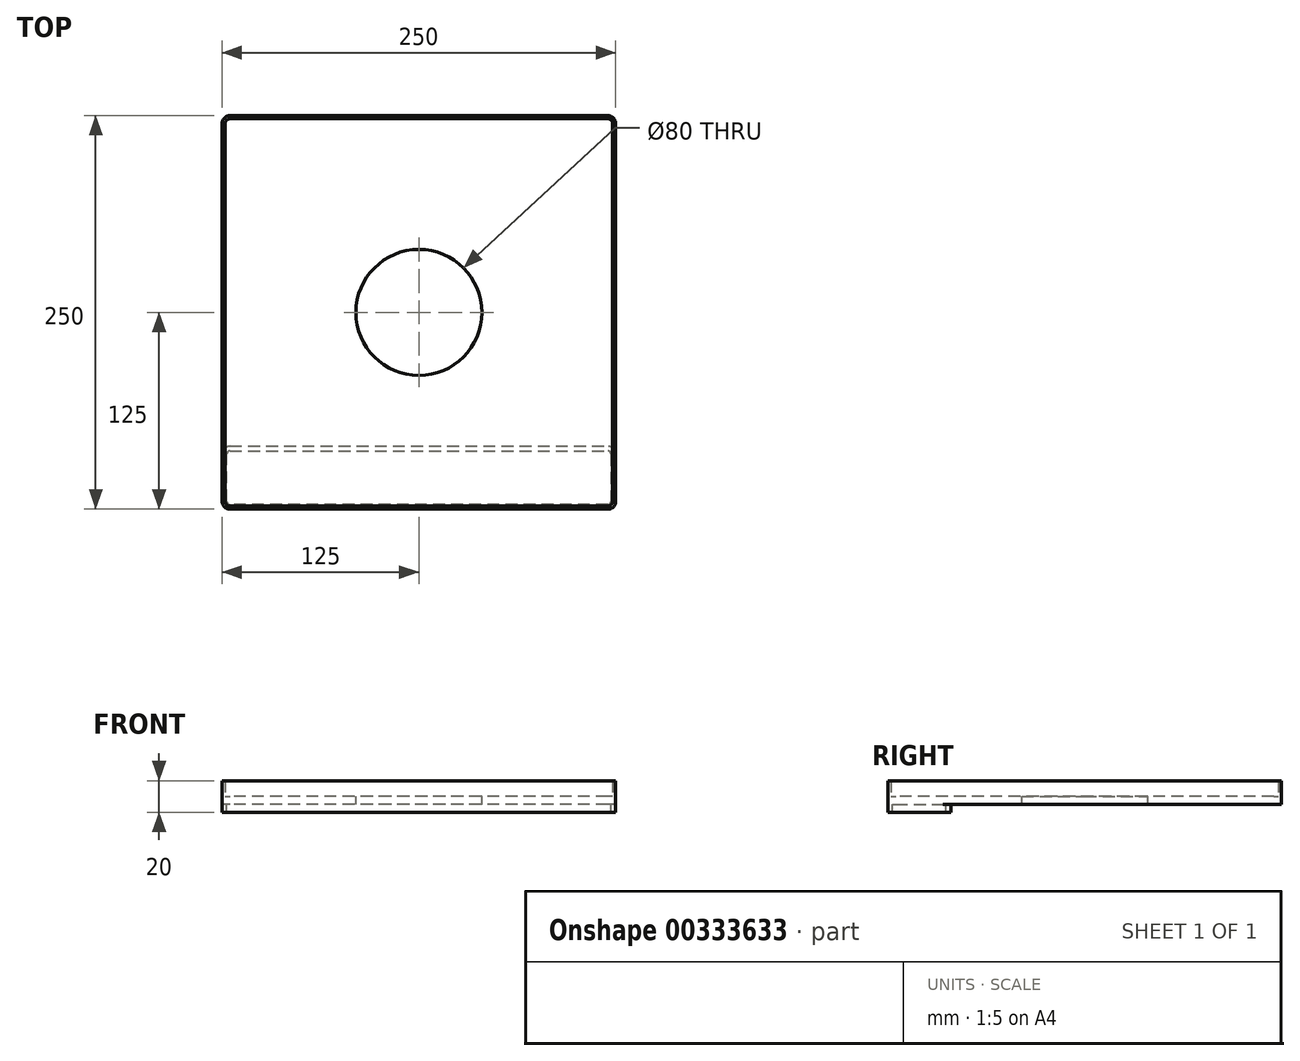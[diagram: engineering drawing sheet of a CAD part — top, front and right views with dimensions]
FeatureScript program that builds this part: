
annotation { "Feature Type Name" : "Feature", "Feature Type Description" : "" }
export const myFeature = defineFeature(function(context is Context, id is Id, definition is map)
    precondition{}
    {
        {
            var Q0;
            Q0=qCreatedBy(makeId("Top.planeOp"),FACE);
            var sketch = newSketch(context, id + "F0", { "sketchPlane" : qUnion([Q0])});
            skLineSegment(sketch, "E0.bottom", {"start": v(120, 125) * mm, "end": v(-120, 125) * mm});
            skLineSegment(sketch, "E0.top", {"start": v(120, -125) * mm, "end": v(-120, -125) * mm});
            skLineSegment(sketch, "E0.left", {"start": v(125, 120) * mm, "end": v(125, -120) * mm});
            skLineSegment(sketch, "E0.right", {"start": v(-125, 120) * mm, "end": v(-125, -120) * mm});
            skPoint(sketch, "E0.middle", {"position": v(0, 0) * mm});
            skPoint(sketch, "E1.visualSharp", {"position": v(-125, -125) * mm});
            skArc(sketch, "E1.filletArc", {"start": v(-125, -120) * mm, "mid": v(-123.54, -123.54) * mm, "end": v(-120, -125) * mm});
            skPoint(sketch, "E2.visualSharp", {"position": v(-125, 125) * mm});
            skArc(sketch, "E2.filletArc", {"start": v(-120, 125) * mm, "mid": v(-123.54, 123.54) * mm, "end": v(-125, 120) * mm});
            skPoint(sketch, "E3.visualSharp", {"position": v(125, 125) * mm});
            skArc(sketch, "E3.filletArc", {"start": v(125, 120) * mm, "mid": v(123.54, 123.54) * mm, "end": v(120, 125) * mm});
            skPoint(sketch, "E4.visualSharp", {"position": v(125, -125) * mm});
            skArc(sketch, "E4.filletArc", {"start": v(120, -125) * mm, "mid": v(123.54, -123.54) * mm, "end": v(125, -120) * mm});
            skSolve(sketch);
        }
        {
            var Q0;
            Q0=makeQuery(id+"F0.imprint","IMPRINT",FACE,{"disambiguationData":[TD([[makeQuery(id+"F0.imprint","IMPRINT",EDGE,{"derivedFrom":sQuery(id+"F0.wireOp",EDGE,"E0.bottom")}),1.0]])]});
            extrude(context, id + "F1", {"entities" : qUnion([Q0]), "depth" : 5 * mm});
        }
        {
            var Q0;
            Q0=makeQuery(id+"F1.opExtrude","CAP_FACE",FACE,{"disambiguationData":[OSD([sQuery(id+"F0.wireOp",EDGE,"E0.bottom"),sQuery(id+"F0.wireOp",EDGE,"E0.top"),sQuery(id+"F0.wireOp",EDGE,"E0.left"),sQuery(id+"F0.wireOp",EDGE,"E0.right"),sQuery(id+"F0.wireOp",EDGE,"E1.filletArc"),sQuery(id+"F0.wireOp",EDGE,"E2.filletArc"),sQuery(id+"F0.wireOp",EDGE,"E3.filletArc"),sQuery(id+"F0.wireOp",EDGE,"E4.filletArc")])],"isStart":false});
            var sketch = newSketch(context, id + "F2", { "sketchPlane" : qUnion([Q0])});
            skLineSegment(sketch, "E5.0", {"start": v(-125, 120) * mm, "end": v(-125, -120) * mm});
            skArc(sketch, "E5.1", {"start": v(-125, -120) * mm, "mid": v(-123.54, -123.54) * mm, "end": v(-120, -125) * mm});
            skLineSegment(sketch, "E5.2", {"start": v(120, -125) * mm, "end": v(-120, -125) * mm});
            skArc(sketch, "E5.3", {"start": v(120, -125) * mm, "mid": v(123.54, -123.54) * mm, "end": v(125, -120) * mm});
            skLineSegment(sketch, "E5.4", {"start": v(125, 120) * mm, "end": v(125, -120) * mm});
            skArc(sketch, "E5.5", {"start": v(125, 120) * mm, "mid": v(123.54, 123.54) * mm, "end": v(120, 125) * mm});
            skLineSegment(sketch, "E5.6", {"start": v(120, 125) * mm, "end": v(-120, 125) * mm});
            skArc(sketch, "E5.7", {"start": v(-120, 125) * mm, "mid": v(-123.54, 123.54) * mm, "end": v(-125, 120) * mm});
            skLineSegment(sketch, "E6.0", {"start": v(120, 123) * mm, "end": v(-120, 123) * mm});
            skArc(sketch, "E6.1", {"start": v(123, 120) * mm, "mid": v(122.12, 122.12) * mm, "end": v(120, 123) * mm});
            skArc(sketch, "E6.2", {"start": v(-120, 123) * mm, "mid": v(-122.12, 122.12) * mm, "end": v(-123, 120) * mm});
            skLineSegment(sketch, "E6.3", {"start": v(123, 120) * mm, "end": v(123, -120) * mm});
            skLineSegment(sketch, "E6.4", {"start": v(-123, 120) * mm, "end": v(-123, -120) * mm});
            skArc(sketch, "E6.5", {"start": v(-123, -120) * mm, "mid": v(-122.12, -122.12) * mm, "end": v(-120, -123) * mm});
            skLineSegment(sketch, "E6.6", {"start": v(120, -123) * mm, "end": v(-120, -123) * mm});
            skArc(sketch, "E6.7", {"start": v(120, -123) * mm, "mid": v(122.12, -122.12) * mm, "end": v(123, -120) * mm});
            skSolve(sketch);
        }
        {
            var Q0;
            Q0=makeQuery(id+"F2.imprint","IMPRINT",FACE,{"disambiguationData":[TD([[makeQuery(id+"F2.imprint","IMPRINT",EDGE,{"derivedFrom":sQuery(id+"F2.wireOp",EDGE,"E5.0")}),1.0]])]});
            extrude(context, id + "F3", {"entities" : qUnion([Q0]), "operationType" : NewBodyOperationType.ADD, "depth" : 10 * mm});
        }
        {
            var Q0;
            Q0=makeQuery(id+"F1.opExtrude","CAP_FACE",FACE,{"disambiguationData":[OSD([sQuery(id+"F0.wireOp",EDGE,"E0.bottom"),sQuery(id+"F0.wireOp",EDGE,"E0.top"),sQuery(id+"F0.wireOp",EDGE,"E0.left"),sQuery(id+"F0.wireOp",EDGE,"E0.right"),sQuery(id+"F0.wireOp",EDGE,"E1.filletArc"),sQuery(id+"F0.wireOp",EDGE,"E2.filletArc"),sQuery(id+"F0.wireOp",EDGE,"E3.filletArc"),sQuery(id+"F0.wireOp",EDGE,"E4.filletArc")])],"isStart":false});
            var sketch = newSketch(context, id + "F4", { "sketchPlane" : qUnion([Q0])});
            skCircle(sketch, "E7", {"center": v(0, 0) * mm, "radius": 40 * mm});
            skSolve(sketch);
        }
        {
            var Q0;
            Q0=makeQuery(id+"F4.imprint","IMPRINT",FACE,{"disambiguationData":[TD([[makeQuery(id+"F4.imprint","IMPRINT",EDGE,{"derivedFrom":sQuery(id+"F4.wireOp",EDGE,"E7")}),1.0]])]});
            extrude(context, id + "F5", {"entities" : qUnion([Q0]), "operationType" : NewBodyOperationType.REMOVE, "endBound" : BoundingType.THROUGH_ALL, "oppositeDirection" : true, "depth" : 25 * mm});
        }
        {
            var Q0;
            Q0=makeQuery(id+"F1.opExtrude","CAP_FACE",FACE,{"disambiguationData":[OSD([sQuery(id+"F0.wireOp",EDGE,"E0.bottom"),sQuery(id+"F0.wireOp",EDGE,"E0.top"),sQuery(id+"F0.wireOp",EDGE,"E0.left"),sQuery(id+"F0.wireOp",EDGE,"E0.right"),sQuery(id+"F0.wireOp",EDGE,"E1.filletArc"),sQuery(id+"F0.wireOp",EDGE,"E2.filletArc"),sQuery(id+"F0.wireOp",EDGE,"E3.filletArc"),sQuery(id+"F0.wireOp",EDGE,"E4.filletArc")])],"isStart":true});
            var sketch = newSketch(context, id + "F6", { "sketchPlane" : qUnion([Q0])});
            skArc(sketch, "E8.0", {"start": v(-125, 120) * mm, "mid": v(-123.54, 123.54) * mm, "end": v(-120, 125) * mm});
            skLineSegment(sketch, "E8.1", {"start": v(120, 125) * mm, "end": v(-120, 125) * mm});
            skArc(sketch, "E8.2", {"start": v(120, 125) * mm, "mid": v(123.54, 123.54) * mm, "end": v(125, 120) * mm});
            skLineSegment(sketch, "E9", {"start": v(-125, 120) * mm, "end": v(-125, 90) * mm});
            skLineSegment(sketch, "E10", {"start": v(-120, 85) * mm, "end": v(120, 85) * mm});
            skLineSegment(sketch, "E11", {"start": v(125, 90) * mm, "end": v(125, 120) * mm});
            skPoint(sketch, "E12.visualSharp", {"position": v(-125, 85) * mm});
            skArc(sketch, "E12.filletArc", {"start": v(-125, 90) * mm, "mid": v(-123.54, 86.46) * mm, "end": v(-120, 85) * mm});
            skPoint(sketch, "E13.visualSharp", {"position": v(125, 85) * mm});
            skArc(sketch, "E13.filletArc", {"start": v(120, 85) * mm, "mid": v(123.54, 86.46) * mm, "end": v(125, 90) * mm});
            skLineSegment(sketch, "E14.0", {"start": v(-122, 120) * mm, "end": v(-122, 90) * mm});
            skArc(sketch, "E14.1", {"start": v(-122, 90) * mm, "mid": v(-121.41, 88.59) * mm, "end": v(-120, 88) * mm});
            skArc(sketch, "E14.2", {"start": v(-122, 120) * mm, "mid": v(-121.41, 121.41) * mm, "end": v(-120, 122) * mm});
            skLineSegment(sketch, "E14.3", {"start": v(-120, 88) * mm, "end": v(120, 88) * mm});
            skLineSegment(sketch, "E14.4", {"start": v(120, 122) * mm, "end": v(-120, 122) * mm});
            skArc(sketch, "E14.5", {"start": v(120, 122) * mm, "mid": v(121.41, 121.41) * mm, "end": v(122, 120) * mm});
            skLineSegment(sketch, "E14.6", {"start": v(122, 90) * mm, "end": v(122, 120) * mm});
            skArc(sketch, "E14.7", {"start": v(120, 88) * mm, "mid": v(121.41, 88.59) * mm, "end": v(122, 90) * mm});
            skSolve(sketch);
        }
        {
            var Q0;
            Q0=makeQuery(id+"F6.imprint","IMPRINT",FACE,{"disambiguationData":[TD([[makeQuery(id+"F6.imprint","IMPRINT",EDGE,{"derivedFrom":sQuery(id+"F6.wireOp",EDGE,"E8.0")}),-1.0]])]});
            extrude(context, id + "F7", {"entities" : qUnion([Q0]), "operationType" : NewBodyOperationType.ADD, "depth" : 5 * mm});
        }
    });
